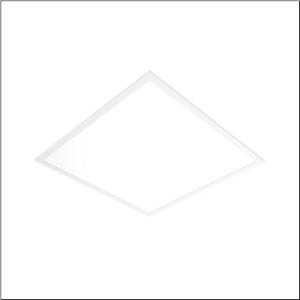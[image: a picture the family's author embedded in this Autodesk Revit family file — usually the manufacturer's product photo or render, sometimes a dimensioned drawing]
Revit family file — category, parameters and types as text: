
# Revit family: apollon_r__41_51mh11wd2n43_c469
name_source: partatom
category: Lighting Fixtures
units: mm (PartAtom-declared; Revit-internal decimal feet)

## family parameters
Cut with Voids When Loaded = No
Host = Face
Light Source = No
Part Type = Normal
Room Calculation Point = No
Round Connector Dimension = Use Diameter
Shared = No

## types (1)
- --- (1 x LED, 3450 lm, 28.5 W, 6500K)
    Apparent Load = 29 VA
    CIE Flux Codes = 61 87 97 100 100
    Color Rendering = 80
    Color Temperature = 6500K
    Default Elevation = 1800 mm
    Description = Apollon® 41, office luminaire, primary optical cover: prismatic diffuser, of PS, light emission: direct distribution, primary light characteristic: symmetric, installation type: lay-in mounting, LED, rated luminous flux: 3.500lm, luminous efficacy: 123lm/W, light colour: 840/865, colour temperature: 4000/6500K, with terminal, 5-pole, mains connection: 220..240V, AC/DC, 0/50..60Hz, housing, of aluminium section, traffic white (RAL 9016), module: M625, length: 620mm, width: 620mm, height: 28mm, housing upper side, of sheet steel, protection rating (complete): IP20, protection rating (lamp compartment, on room side): IP40, insulation class (complete): insulation class II (safety insulation), certification: CE, ENEC, permissible operating ambient temperature: -25..+40°C, packaging unit: 1 piece
    Height = 0 mm  [stored 0 ft]
    Lamp = 1 x LED
    Lamp Light Flux = 3450 lm
    Lamp Power = 28.5 W
    Lamp count = 1
    Length = 620 mm
    Luminous efficacy = 121 lm/W
    Manufacturer = Siteco
    ModVariant = No
    Model = 51MH11WD2N43
    Mounting Place = Ceiling
    Mounting Type = Recessed
    Number of Poles = 1
    OnlyDefault = Yes
    Power Factor = 1
    Product Name = Apollon® 41
    Product group = office luminaire | ceiling recessed
    ProductGroupID = 400
    Protection Class = Protection class II
    Protection Degree = IP 20
    RLX_Detail_Level = 1
    RLX_Emergency_Light_Flux = 0 lm
    RLX_Emergency_Type = 0
    RLX_Emergency_Type_DB = No
    RlxData = <blob elided: 12405 chars, md5=58c4125e>
    Socket = socket
    Standby Power = 0 W
    System Light Flux = 3450 lm
    System Power = 29 W
    Type Comments = individual setting
    Type Image = l_1291024.jpg
    URL = http://relux.com
    VarID = @adj_045603
    Voltage = 0 V
    Weight = 0.00 kg
    Width = 620 mm

note: [stored X ft] marks values corroborated as IEEE doubles in the binary element streams (Revit-internal decimal feet)

## geometry (parser evidence)
native form markers: Sweep x8
no freeform markers — native parametric forms only
